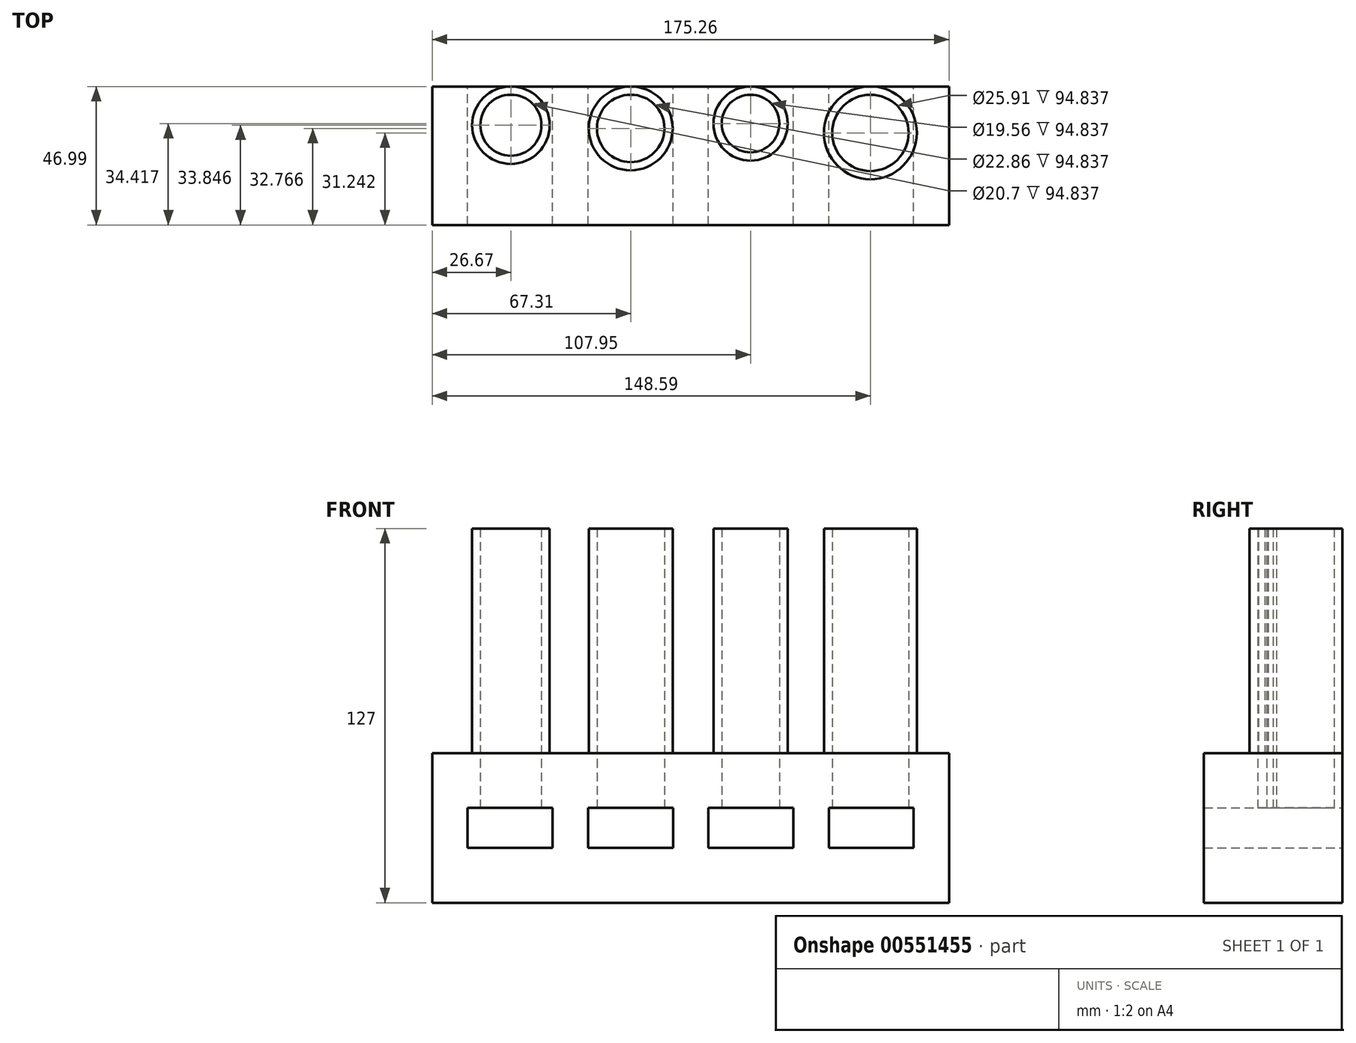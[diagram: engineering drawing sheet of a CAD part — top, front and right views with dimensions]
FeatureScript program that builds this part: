
annotation { "Feature Type Name" : "Feature", "Feature Type Description" : "" }
export const myFeature = defineFeature(function(context is Context, id is Id, definition is map)
    precondition{}
    {
        {
            var Q0;
            Q0=qCreatedBy(makeId("Front.planeOp"),FACE);
            var sketch = newSketch(context, id + "F0", { "sketchPlane" : qUnion([Q0])});
            skLineSegment(sketch, "E0.bottom", {"start": v(87.63, 25.4) * mm, "end": v(-87.63, 25.4) * mm});
            skLineSegment(sketch, "E0.top", {"start": v(87.63, -25.4) * mm, "end": v(-87.63, -25.4) * mm});
            skLineSegment(sketch, "E0.left", {"start": v(87.63, 25.4) * mm, "end": v(87.63, -25.4) * mm});
            skLineSegment(sketch, "E0.right", {"start": v(-87.63, 25.4) * mm, "end": v(-87.63, -25.4) * mm});
            skPoint(sketch, "E0.middle", {"position": v(0, 0) * mm});
            skLineSegment(sketch, "E1", {"start": v(-87.63, 0) * mm, "end": v(87.63, 0) * mm, "construction": true});
            skLineSegment(sketch, "E2", {"start": v(87.63, 0) * mm, "end": v(87.63, -6.76) * mm, "construction": true});
            skLineSegment(sketch, "E3", {"start": v(87.63, -6.76) * mm, "end": v(-87.63, -6.76) * mm, "construction": true});
            skLineSegment(sketch, "E4", {"start": v(-87.63, -6.76) * mm, "end": v(-87.63, 6.76) * mm, "construction": true});
            skLineSegment(sketch, "E5", {"start": v(-87.63, 6.76) * mm, "end": v(87.63, 6.76) * mm, "construction": true});
            skLineSegment(sketch, "E6", {"start": v(-87.63, 6.76) * mm, "end": v(-75.62, 6.76) * mm, "construction": true});
            skLineSegment(sketch, "E7.bottom", {"start": v(-75.62, 6.76) * mm, "end": v(-46.79, 6.76) * mm});
            skLineSegment(sketch, "E7.top", {"start": v(-75.62, -6.76) * mm, "end": v(-46.79, -6.76) * mm});
            skLineSegment(sketch, "E7.left", {"start": v(-75.62, 6.76) * mm, "end": v(-75.62, -6.76) * mm});
            skLineSegment(sketch, "E7.right", {"start": v(-46.79, 6.76) * mm, "end": v(-46.79, -6.76) * mm});
            skLineSegment(sketch, "E8", {"start": v(-46.79, 6.76) * mm, "end": v(-34.77, 6.76) * mm, "construction": true});
            skLineSegment(sketch, "E9.bottom", {"start": v(-34.77, 6.76) * mm, "end": v(-5.94, 6.76) * mm});
            skLineSegment(sketch, "E9.top", {"start": v(-34.77, -6.76) * mm, "end": v(-5.94, -6.76) * mm});
            skLineSegment(sketch, "E9.left", {"start": v(-34.77, 6.76) * mm, "end": v(-34.77, -6.76) * mm});
            skLineSegment(sketch, "E9.right", {"start": v(-5.94, 6.76) * mm, "end": v(-5.94, -6.76) * mm});
            skLineSegment(sketch, "E10", {"start": v(-5.94, 6.76) * mm, "end": v(6.07, 6.76) * mm, "construction": true});
            skLineSegment(sketch, "E11", {"start": v(6.07, 6.76) * mm, "end": v(6.07, -6.76) * mm});
            skLineSegment(sketch, "E12", {"start": v(6.07, -6.76) * mm, "end": v(34.84, -6.76) * mm});
            skLineSegment(sketch, "E13", {"start": v(34.84, -6.76) * mm, "end": v(34.84, 6.76) * mm});
            skLineSegment(sketch, "E14", {"start": v(34.84, 6.76) * mm, "end": v(6.07, 6.76) * mm});
            skLineSegment(sketch, "E15", {"start": v(34.84, 6.76) * mm, "end": v(46.85, 6.76) * mm, "construction": true});
            skLineSegment(sketch, "E16.bottom", {"start": v(46.85, 6.76) * mm, "end": v(75.62, 6.76) * mm});
            skLineSegment(sketch, "E16.top", {"start": v(46.85, -6.76) * mm, "end": v(75.62, -6.76) * mm});
            skLineSegment(sketch, "E16.left", {"start": v(46.85, 6.76) * mm, "end": v(46.85, -6.76) * mm});
            skLineSegment(sketch, "E16.right", {"start": v(75.62, 6.76) * mm, "end": v(75.62, -6.76) * mm});
            skSolve(sketch);
        }
        {
            var Q0;
            Q0 = qSketchRegion(id + "F0", true);
            extrude(context, id + "F1", {"entities" : qUnion([Q0]), "depth" : 47 * mm, "offsetDistance" : 25.4 * mm});
        }
        {
            var Q0;
            Q0=makeQuery(id+"F1.opExtrude","SWEPT_FACE",FACE,{"disambiguationData":[OSD([sQuery(id+"F0.wireOp",EDGE,"E0.bottom")])]});
            var sketch = newSketch(context, id + "F2", { "sketchPlane" : qUnion([Q0])});
            skLineSegment(sketch, "E17", {"start": v(87.63, 0) * mm, "end": v(74.93, 0) * mm, "construction": true});
            skLineSegment(sketch, "E18", {"start": v(74.93, 0) * mm, "end": v(47, 0) * mm, "construction": true});
            skCircle(sketch, "E19", {"center": v(60.96, -15.75) * mm, "radius": 12.95 * mm});
            skCircle(sketch, "E20", {"center": v(60.96, -15.75) * mm, "radius": 15.75 * mm});
            skSolve(sketch);
        }
        {
            var Q0;
            Q0=makeQuery(id+"F2.imprint","IMPRINT",FACE,{"disambiguationData":[TD([[makeQuery(id+"F2.imprint","IMPRINT",EDGE,{"derivedFrom":sQuery(id+"F2.wireOp",EDGE,"E19")}),-1.0]])]});
            extrude(context, id + "F3", {"entities" : qUnion([Q0]), "operationType" : NewBodyOperationType.ADD, "depth" : 76.2 * mm, "offsetDistance" : 25.4 * mm});
        }
        {
            var Q0;
            Q0=makeQuery(id+"F3.boolean.opBoolean","SPLIT",FACE,{"disambiguationData":[TD([makeQuery(id+"F3.opExtrude","SWEPT_FACE",FACE,{"disambiguationData":[OSD([sQuery(id+"F2.wireOp",EDGE,"E19")])]})])],"derivedFrom":makeQuery(id+"F1.opExtrude","SWEPT_FACE",FACE,{"disambiguationData":[OSD([sQuery(id+"F0.wireOp",EDGE,"E0.bottom")])]})});
            extrude(context, id + "F4", {"entities" : qUnion([Q0]), "operationType" : NewBodyOperationType.REMOVE, "oppositeDirection" : true, "depth" : 25.4 * mm, "offsetDistance" : 25.4 * mm});
        }
        {
            var Q0;
            {var subQ1=sQuery(id+"F0.wireOp",EDGE,"E0.left");var subQ19=sQuery(id+"F0.wireOp",EDGE,"E0.bottom");Q0=makeQuery(id+"F3.boolean.opBoolean","SPLIT",FACE,{"disambiguationData":[TD([makeQuery(id+"F1.opExtrude","SWEPT_FACE",FACE,{"disambiguationData":[OSD([subQ1])]})])],"derivedFrom":makeQuery(id+"F1.opExtrude","SWEPT_FACE",FACE,{"disambiguationData":[OSD([subQ19])]})});}
            var sketch = newSketch(context, id + "F5", { "sketchPlane" : qUnion([Q0])});
            skLineSegment(sketch, "E21", {"start": v(87.63, 0) * mm, "end": v(34.3, 0) * mm, "construction": true});
            skLineSegment(sketch, "E22", {"start": v(34.3, 0) * mm, "end": v(20.32, 0) * mm, "construction": true});
            skCircle(sketch, "E23", {"center": v(20.32, -12.57) * mm, "radius": 9.78 * mm});
            skCircle(sketch, "E24", {"center": v(20.32, -12.57) * mm, "radius": 12.57 * mm});
            skSolve(sketch);
        }
        {
            var Q0;
            Q0 = qSketchRegion(id + "F5", true);
            extrude(context, id + "F6", {"entities" : qUnion([Q0]), "operationType" : NewBodyOperationType.ADD, "depth" : 76.2 * mm, "offsetDistance" : 25.4 * mm});
        }
        {
            var Q0;
            {var subQ1=sQuery(id+"F0.wireOp",EDGE,"E0.left");var subQ19=sQuery(id+"F0.wireOp",EDGE,"E0.bottom");Q0=makeQuery(id+"F6.boolean.opBoolean","SPLIT",FACE,{"disambiguationData":[TD([makeQuery(id+"F6.opExtrude","SWEPT_FACE",FACE,{"disambiguationData":[OSD([sQuery(id+"F5.wireOp",EDGE,"E23")])]})])],"derivedFrom":makeQuery(id+"F3.boolean.opBoolean","SPLIT",FACE,{"disambiguationData":[TD([makeQuery(id+"F1.opExtrude","SWEPT_FACE",FACE,{"disambiguationData":[OSD([subQ1])]})])],"derivedFrom":makeQuery(id+"F1.opExtrude","SWEPT_FACE",FACE,{"disambiguationData":[OSD([subQ19])]})})});}
            extrude(context, id + "F7", {"entities" : qUnion([Q0]), "operationType" : NewBodyOperationType.REMOVE, "oppositeDirection" : true, "depth" : 25.4 * mm, "offsetDistance" : 25.4 * mm});
        }
        {
            var Q0;
            {var subQ2=sQuery(id+"F0.wireOp",EDGE,"E0.left");var subQ3=makeQuery(id+"F1.opExtrude","SWEPT_FACE",FACE,{"disambiguationData":[OSD([subQ2])]});var subQ22=sQuery(id+"F0.wireOp",EDGE,"E0.bottom");Q0=makeQuery(id+"F6.boolean.opBoolean","SPLIT",FACE,{"disambiguationData":[TD([subQ3])],"derivedFrom":makeQuery(id+"F3.boolean.opBoolean","SPLIT",FACE,{"disambiguationData":[TD([subQ3])],"derivedFrom":makeQuery(id+"F1.opExtrude","SWEPT_FACE",FACE,{"disambiguationData":[OSD([subQ22])]})})});}
            var sketch = newSketch(context, id + "F8", { "sketchPlane" : qUnion([Q0])});
            skLineSegment(sketch, "E25", {"start": v(0, 0) * mm, "end": v(87.63, 0) * mm, "construction": true});
            skLineSegment(sketch, "E26", {"start": v(0, 0) * mm, "end": v(-6.35, 0) * mm, "construction": true});
            skLineSegment(sketch, "E27", {"start": v(-6.35, 0) * mm, "end": v(-20.32, 0) * mm, "construction": true});
            skCircle(sketch, "E28", {"center": v(-20.32, -14.22) * mm, "radius": 11.43 * mm});
            skCircle(sketch, "E29", {"center": v(-20.32, -14.22) * mm, "radius": 14.22 * mm});
            skSolve(sketch);
        }
        {
            var Q0;
            Q0=makeQuery(id+"F8.imprint","IMPRINT",FACE,{"disambiguationData":[TD([[makeQuery(id+"F8.imprint","IMPRINT",EDGE,{"derivedFrom":sQuery(id+"F8.wireOp",EDGE,"E28")}),-1.0]])]});
            extrude(context, id + "F9", {"entities" : qUnion([Q0]), "operationType" : NewBodyOperationType.ADD, "depth" : 76.2 * mm, "offsetDistance" : 25.4 * mm});
        }
        {
            var Q0;
            {var subQ2=sQuery(id+"F0.wireOp",EDGE,"E0.left");var subQ3=makeQuery(id+"F1.opExtrude","SWEPT_FACE",FACE,{"disambiguationData":[OSD([subQ2])]});var subQ22=sQuery(id+"F0.wireOp",EDGE,"E0.bottom");Q0=makeQuery(id+"F9.boolean.opBoolean","SPLIT",FACE,{"disambiguationData":[TD([makeQuery(id+"F9.opExtrude","SWEPT_FACE",FACE,{"disambiguationData":[OSD([sQuery(id+"F8.wireOp",EDGE,"E28")])]})])],"derivedFrom":makeQuery(id+"F6.boolean.opBoolean","SPLIT",FACE,{"disambiguationData":[TD([subQ3])],"derivedFrom":makeQuery(id+"F3.boolean.opBoolean","SPLIT",FACE,{"disambiguationData":[TD([subQ3])],"derivedFrom":makeQuery(id+"F1.opExtrude","SWEPT_FACE",FACE,{"disambiguationData":[OSD([subQ22])]})})})});}
            extrude(context, id + "F10", {"entities" : qUnion([Q0]), "operationType" : NewBodyOperationType.REMOVE, "oppositeDirection" : true, "depth" : 25.4 * mm, "offsetDistance" : 25.4 * mm});
        }
        {
            var Q0;
            {var subQ2=sQuery(id+"F0.wireOp",EDGE,"E0.left");var subQ3=makeQuery(id+"F1.opExtrude","SWEPT_FACE",FACE,{"disambiguationData":[OSD([subQ2])]});var subQ22=sQuery(id+"F0.wireOp",EDGE,"E0.bottom");Q0=makeQuery(id+"F9.boolean.opBoolean","SPLIT",FACE,{"disambiguationData":[TD([subQ3])],"derivedFrom":makeQuery(id+"F6.boolean.opBoolean","SPLIT",FACE,{"disambiguationData":[TD([subQ3])],"derivedFrom":makeQuery(id+"F3.boolean.opBoolean","SPLIT",FACE,{"disambiguationData":[TD([subQ3])],"derivedFrom":makeQuery(id+"F1.opExtrude","SWEPT_FACE",FACE,{"disambiguationData":[OSD([subQ22])]})})})});}
            var sketch = newSketch(context, id + "F11", { "sketchPlane" : qUnion([Q0])});
            skCircle(sketch, "E30", {"center": v(-60.96, -13.14) * mm, "radius": 13.14 * mm});
            skCircle(sketch, "E31", {"center": v(-60.96, -13.14) * mm, "radius": 10.35 * mm});
            skSolve(sketch);
        }
        {
            var Q0;
            Q0 = qSketchRegion(id + "F11", true);
            extrude(context, id + "F12", {"entities" : qUnion([Q0]), "operationType" : NewBodyOperationType.ADD, "depth" : 76.2 * mm, "offsetDistance" : 25.4 * mm});
        }
        {
            var Q0;
            {var subQ2=sQuery(id+"F0.wireOp",EDGE,"E0.left");var subQ3=makeQuery(id+"F1.opExtrude","SWEPT_FACE",FACE,{"disambiguationData":[OSD([subQ2])]});var subQ22=sQuery(id+"F0.wireOp",EDGE,"E0.bottom");Q0=makeQuery(id+"F12.boolean.opBoolean","SPLIT",FACE,{"disambiguationData":[TD([makeQuery(id+"F12.opExtrude","SWEPT_FACE",FACE,{"disambiguationData":[OSD([sQuery(id+"F11.wireOp",EDGE,"E31")])]})])],"derivedFrom":makeQuery(id+"F9.boolean.opBoolean","SPLIT",FACE,{"disambiguationData":[TD([subQ3])],"derivedFrom":makeQuery(id+"F6.boolean.opBoolean","SPLIT",FACE,{"disambiguationData":[TD([subQ3])],"derivedFrom":makeQuery(id+"F3.boolean.opBoolean","SPLIT",FACE,{"disambiguationData":[TD([subQ3])],"derivedFrom":makeQuery(id+"F1.opExtrude","SWEPT_FACE",FACE,{"disambiguationData":[OSD([subQ22])]})})})})});}
            extrude(context, id + "F13", {"entities" : qUnion([Q0]), "operationType" : NewBodyOperationType.REMOVE, "oppositeDirection" : true, "depth" : 25.4 * mm, "offsetDistance" : 25.4 * mm});
        }
    });
